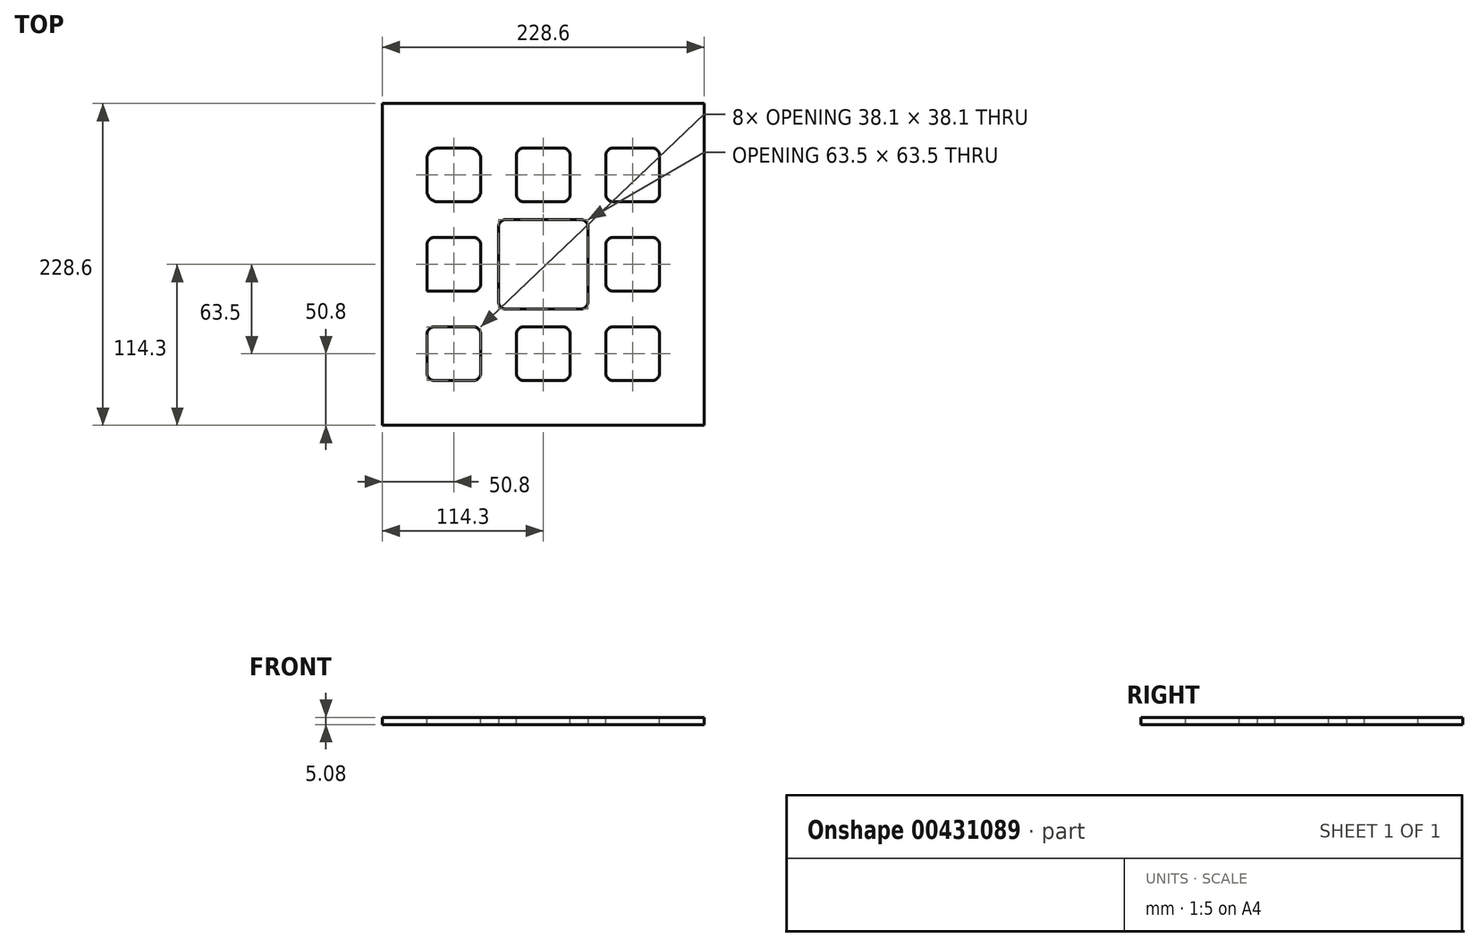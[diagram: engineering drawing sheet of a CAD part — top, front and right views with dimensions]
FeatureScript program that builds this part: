
annotation { "Feature Type Name" : "Feature", "Feature Type Description" : "" }
export const myFeature = defineFeature(function(context is Context, id is Id, definition is map)
    precondition{}
    {
        {
            var Q0;
            Q0=qCreatedBy(makeId("Top.planeOp"),FACE);
            var sketch = newSketch(context, id + "F0", { "sketchPlane" : qUnion([Q0])});
            skLineSegment(sketch, "E0.bottom", {"start": v(114.3, 114.3) * mm, "end": v(-114.3, 114.3) * mm});
            skLineSegment(sketch, "E0.top", {"start": v(114.3, -114.3) * mm, "end": v(-114.3, -114.3) * mm});
            skLineSegment(sketch, "E0.left", {"start": v(114.3, 114.3) * mm, "end": v(114.3, -114.3) * mm});
            skLineSegment(sketch, "E0.right", {"start": v(-114.3, 114.3) * mm, "end": v(-114.3, -114.3) * mm});
            skPoint(sketch, "E0.middle", {"position": v(0, 0) * mm});
            skLineSegment(sketch, "E1.bottom", {"start": v(31.75, 31.75) * mm, "end": v(-31.75, 31.75) * mm});
            skLineSegment(sketch, "E1.top", {"start": v(31.75, -31.75) * mm, "end": v(-31.75, -31.75) * mm});
            skLineSegment(sketch, "E1.left", {"start": v(31.75, 31.75) * mm, "end": v(31.75, -31.75) * mm});
            skLineSegment(sketch, "E1.right", {"start": v(-31.75, 31.75) * mm, "end": v(-31.75, -31.75) * mm});
            skSolve(sketch);
        }
        {
            var Q0;
            Q0 = qSketchRegion(id + "F0", true);
            extrude(context, id + "F1", {"entities" : qUnion([Q0]), "depth" : 5.08 * mm});
        }
        {
            var Q0;
            Q0=makeQuery(id+"F1.opExtrude","CAP_FACE",FACE,{"disambiguationData":[OSD([sQuery(id+"F0.wireOp",EDGE,"E0.bottom"),sQuery(id+"F0.wireOp",EDGE,"E0.top"),sQuery(id+"F0.wireOp",EDGE,"E0.left"),sQuery(id+"F0.wireOp",EDGE,"E0.right"),sQuery(id+"F0.wireOp",EDGE,"E1.bottom"),sQuery(id+"F0.wireOp",EDGE,"E1.top"),sQuery(id+"F0.wireOp",EDGE,"E1.left"),sQuery(id+"F0.wireOp",EDGE,"E1.right")])],"isStart":false});
            var sketch = newSketch(context, id + "F2", { "sketchPlane" : qUnion([Q0])});
            skLineSegment(sketch, "E2.bottom", {"start": v(-44.45, 82.55) * mm, "end": v(-82.55, 82.55) * mm});
            skLineSegment(sketch, "E2.top", {"start": v(-44.45, 44.45) * mm, "end": v(-82.55, 44.45) * mm});
            skLineSegment(sketch, "E2.left", {"start": v(-44.45, 82.55) * mm, "end": v(-44.45, 44.45) * mm});
            skLineSegment(sketch, "E2.right", {"start": v(-82.55, 82.55) * mm, "end": v(-82.55, 44.45) * mm});
            skPoint(sketch, "E2.middle", {"position": v(-63.5, 63.5) * mm});
            skSolve(sketch);
        }
        {
            var Q0;
            Q0 = qSketchRegion(id + "F2", true);
            extrude(context, id + "F3", {"entities" : qUnion([Q0]), "operationType" : NewBodyOperationType.REMOVE, "oppositeDirection" : true, "depth" : 25.4 * mm});
        }
        {
            var Q0;
            Q0=makeQuery(id+"F3.boolean.opBoolean","COPY",EDGE,{"derivedFrom":makeQuery(id+"F3.opExtrude","SWEPT_EDGE",EDGE,{"disambiguationData":[OSD([sQuery(id+"F2.wireOp",EDGE,"E2.bottom"),sQuery(id+"F2.wireOp",EDGE,"E2.right")])]})});
            var Q1;
            Q1=makeQuery(id+"F3.boolean.opBoolean","COPY",EDGE,{"derivedFrom":makeQuery(id+"F3.opExtrude","SWEPT_EDGE",EDGE,{"disambiguationData":[OSD([sQuery(id+"F2.wireOp",EDGE,"E2.bottom"),sQuery(id+"F2.wireOp",EDGE,"E2.left")])]})});
            var Q2;
            Q2=makeQuery(id+"F3.boolean.opBoolean","COPY",EDGE,{"derivedFrom":makeQuery(id+"F3.opExtrude","SWEPT_EDGE",EDGE,{"disambiguationData":[OSD([sQuery(id+"F2.wireOp",EDGE,"E2.top"),sQuery(id+"F2.wireOp",EDGE,"E2.left")])]})});
            var Q3;
            Q3=makeQuery(id+"F3.boolean.opBoolean","COPY",EDGE,{"derivedFrom":makeQuery(id+"F3.opExtrude","SWEPT_EDGE",EDGE,{"disambiguationData":[OSD([sQuery(id+"F2.wireOp",EDGE,"E2.top"),sQuery(id+"F2.wireOp",EDGE,"E2.right")])]})});
            fillet(context, id + "F4", {"entities" : qUnion([Q0, Q1, Q2, Q3]), "radius" : 7.62 * mm, "tangentPropagation" : true, "allowEdgeOverflow" : false});
        }
        {
            var Q0;
            Q0=makeQuery(id+"F1.opExtrude","CAP_FACE",FACE,{"disambiguationData":[OSD([sQuery(id+"F0.wireOp",EDGE,"E0.bottom"),sQuery(id+"F0.wireOp",EDGE,"E0.top"),sQuery(id+"F0.wireOp",EDGE,"E0.left"),sQuery(id+"F0.wireOp",EDGE,"E0.right"),sQuery(id+"F0.wireOp",EDGE,"E1.bottom"),sQuery(id+"F0.wireOp",EDGE,"E1.top"),sQuery(id+"F0.wireOp",EDGE,"E1.left"),sQuery(id+"F0.wireOp",EDGE,"E1.right")])],"isStart":false});
            var sketch = newSketch(context, id + "F5", { "sketchPlane" : qUnion([Q0])});
            skLineSegment(sketch, "E3.bottom", {"start": v(19.05, 82.55) * mm, "end": v(-19.05, 82.55) * mm});
            skLineSegment(sketch, "E3.top", {"start": v(19.05, 44.45) * mm, "end": v(-19.05, 44.45) * mm});
            skLineSegment(sketch, "E3.left", {"start": v(19.05, 82.55) * mm, "end": v(19.05, 44.45) * mm});
            skLineSegment(sketch, "E3.right", {"start": v(-19.05, 82.55) * mm, "end": v(-19.05, 44.45) * mm});
            skPoint(sketch, "E3.middle", {"position": v(0, 63.5) * mm});
            skLineSegment(sketch, "E4.bottom", {"start": v(82.55, 82.55) * mm, "end": v(44.45, 82.55) * mm});
            skLineSegment(sketch, "E4.top", {"start": v(82.55, 44.45) * mm, "end": v(44.45, 44.45) * mm});
            skLineSegment(sketch, "E4.left", {"start": v(82.55, 82.55) * mm, "end": v(82.55, 44.45) * mm});
            skLineSegment(sketch, "E4.right", {"start": v(44.45, 82.55) * mm, "end": v(44.45, 44.45) * mm});
            skPoint(sketch, "E4.middle", {"position": v(63.5, 63.5) * mm});
            skLineSegment(sketch, "E5.bottom", {"start": v(82.55, 19.05) * mm, "end": v(44.45, 19.05) * mm});
            skLineSegment(sketch, "E5.top", {"start": v(82.55, -19.05) * mm, "end": v(44.45, -19.05) * mm});
            skLineSegment(sketch, "E5.left", {"start": v(82.55, 19.05) * mm, "end": v(82.55, -19.05) * mm});
            skLineSegment(sketch, "E5.right", {"start": v(44.45, 19.05) * mm, "end": v(44.45, -19.05) * mm});
            skPoint(sketch, "E5.middle", {"position": v(63.5, 0) * mm});
            skLineSegment(sketch, "E6.bottom", {"start": v(82.55, -44.45) * mm, "end": v(44.45, -44.45) * mm});
            skLineSegment(sketch, "E6.top", {"start": v(82.55, -82.55) * mm, "end": v(44.45, -82.55) * mm});
            skLineSegment(sketch, "E6.left", {"start": v(82.55, -44.45) * mm, "end": v(82.55, -82.55) * mm});
            skLineSegment(sketch, "E6.right", {"start": v(44.45, -44.45) * mm, "end": v(44.45, -82.55) * mm});
            skPoint(sketch, "E6.middle", {"position": v(63.5, -63.5) * mm});
            skLineSegment(sketch, "E7.bottom", {"start": v(19.05, -44.45) * mm, "end": v(-19.05, -44.45) * mm});
            skLineSegment(sketch, "E7.top", {"start": v(19.05, -82.55) * mm, "end": v(-19.05, -82.55) * mm});
            skLineSegment(sketch, "E7.left", {"start": v(19.05, -44.45) * mm, "end": v(19.05, -82.55) * mm});
            skLineSegment(sketch, "E7.right", {"start": v(-19.05, -44.45) * mm, "end": v(-19.05, -82.55) * mm});
            skPoint(sketch, "E7.middle", {"position": v(0, -63.5) * mm});
            skLineSegment(sketch, "E8.bottom", {"start": v(-44.45, -44.45) * mm, "end": v(-82.55, -44.45) * mm});
            skLineSegment(sketch, "E8.top", {"start": v(-44.45, -82.55) * mm, "end": v(-82.55, -82.55) * mm});
            skLineSegment(sketch, "E8.left", {"start": v(-44.45, -44.45) * mm, "end": v(-44.45, -82.55) * mm});
            skLineSegment(sketch, "E8.right", {"start": v(-82.55, -44.45) * mm, "end": v(-82.55, -82.55) * mm});
            skPoint(sketch, "E8.middle", {"position": v(-63.5, -63.5) * mm});
            skLineSegment(sketch, "E9.bottom", {"start": v(-44.45, 19.05) * mm, "end": v(-82.55, 19.05) * mm});
            skLineSegment(sketch, "E9.top", {"start": v(-44.45, -19.05) * mm, "end": v(-82.55, -19.05) * mm});
            skLineSegment(sketch, "E9.left", {"start": v(-44.45, 19.05) * mm, "end": v(-44.45, -19.05) * mm});
            skLineSegment(sketch, "E9.right", {"start": v(-82.55, 19.05) * mm, "end": v(-82.55, -19.05) * mm});
            skPoint(sketch, "E9.middle", {"position": v(-63.5, 0) * mm});
            skSolve(sketch);
        }
        {
            var Q0;
            Q0=makeQuery(id+"F5.imprint","IMPRINT",FACE,{"disambiguationData":[TD([[makeQuery(id+"F5.imprint","IMPRINT",EDGE,{"derivedFrom":sQuery(id+"F5.wireOp",EDGE,"E9.bottom")}),1.0]])]});
            var Q1;
            Q1=makeQuery(id+"F5.imprint","IMPRINT",FACE,{"disambiguationData":[TD([[makeQuery(id+"F5.imprint","IMPRINT",EDGE,{"derivedFrom":sQuery(id+"F5.wireOp",EDGE,"E3.bottom")}),1.0]])]});
            var Q2;
            Q2=makeQuery(id+"F5.imprint","IMPRINT",FACE,{"disambiguationData":[TD([[makeQuery(id+"F5.imprint","IMPRINT",EDGE,{"derivedFrom":sQuery(id+"F5.wireOp",EDGE,"E4.bottom")}),1.0]])]});
            var Q3;
            Q3=makeQuery(id+"F5.imprint","IMPRINT",FACE,{"disambiguationData":[TD([[makeQuery(id+"F5.imprint","IMPRINT",EDGE,{"derivedFrom":sQuery(id+"F5.wireOp",EDGE,"E5.bottom")}),1.0]])]});
            var Q4;
            Q4=makeQuery(id+"F5.imprint","IMPRINT",FACE,{"disambiguationData":[TD([[makeQuery(id+"F5.imprint","IMPRINT",EDGE,{"derivedFrom":sQuery(id+"F5.wireOp",EDGE,"E6.bottom")}),1.0]])]});
            var Q5;
            Q5=makeQuery(id+"F5.imprint","IMPRINT",FACE,{"disambiguationData":[TD([[makeQuery(id+"F5.imprint","IMPRINT",EDGE,{"derivedFrom":sQuery(id+"F5.wireOp",EDGE,"E7.bottom")}),1.0]])]});
            var Q6;
            Q6=makeQuery(id+"F5.imprint","IMPRINT",FACE,{"disambiguationData":[TD([[makeQuery(id+"F5.imprint","IMPRINT",EDGE,{"derivedFrom":sQuery(id+"F5.wireOp",EDGE,"E8.bottom")}),1.0]])]});
            extrude(context, id + "F6", {"entities" : qUnion([Q0, Q1, Q2, Q3, Q4, Q5, Q6]), "operationType" : NewBodyOperationType.REMOVE, "oppositeDirection" : true, "depth" : 25.4 * mm});
        }
        {
            var Q0;
            Q0=makeQuery(id+"F6.boolean.opBoolean","COPY",EDGE,{"derivedFrom":makeQuery(id+"F6.opExtrude","SWEPT_EDGE",EDGE,{"disambiguationData":[OSD([sQuery(id+"F5.wireOp",EDGE,"E9.bottom"),sQuery(id+"F5.wireOp",EDGE,"E9.right")])]})});
            var Q1;
            Q1=makeQuery(id+"F6.boolean.opBoolean","COPY",EDGE,{"derivedFrom":makeQuery(id+"F6.opExtrude","SWEPT_EDGE",EDGE,{"disambiguationData":[OSD([sQuery(id+"F5.wireOp",EDGE,"E8.bottom"),sQuery(id+"F5.wireOp",EDGE,"E8.right")])]})});
            var Q2;
            Q2=makeQuery(id+"F1.opExtrude","SWEPT_EDGE",EDGE,{"disambiguationData":[OSD([sQuery(id+"F0.wireOp",EDGE,"E1.bottom"),sQuery(id+"F0.wireOp",EDGE,"E1.right")])]});
            var Q3;
            Q3=makeQuery(id+"F6.boolean.opBoolean","COPY",EDGE,{"derivedFrom":makeQuery(id+"F6.opExtrude","SWEPT_EDGE",EDGE,{"disambiguationData":[OSD([sQuery(id+"F5.wireOp",EDGE,"E3.bottom"),sQuery(id+"F5.wireOp",EDGE,"E3.right")])]})});
            var Q4;
            Q4=makeQuery(id+"F6.boolean.opBoolean","COPY",EDGE,{"derivedFrom":makeQuery(id+"F6.opExtrude","SWEPT_EDGE",EDGE,{"disambiguationData":[OSD([sQuery(id+"F5.wireOp",EDGE,"E5.bottom"),sQuery(id+"F5.wireOp",EDGE,"E5.right")])]})});
            var Q5;
            Q5=makeQuery(id+"F6.boolean.opBoolean","COPY",EDGE,{"derivedFrom":makeQuery(id+"F6.opExtrude","SWEPT_EDGE",EDGE,{"disambiguationData":[OSD([sQuery(id+"F5.wireOp",EDGE,"E4.bottom"),sQuery(id+"F5.wireOp",EDGE,"E4.right")])]})});
            var Q6;
            Q6=makeQuery(id+"F6.boolean.opBoolean","COPY",EDGE,{"derivedFrom":makeQuery(id+"F6.opExtrude","SWEPT_EDGE",EDGE,{"disambiguationData":[OSD([sQuery(id+"F5.wireOp",EDGE,"E6.bottom"),sQuery(id+"F5.wireOp",EDGE,"E6.right")])]})});
            var Q7;
            Q7=makeQuery(id+"F6.boolean.opBoolean","COPY",EDGE,{"derivedFrom":makeQuery(id+"F6.opExtrude","SWEPT_EDGE",EDGE,{"disambiguationData":[OSD([sQuery(id+"F5.wireOp",EDGE,"E7.bottom"),sQuery(id+"F5.wireOp",EDGE,"E7.right")])]})});
            var Q8;
            Q8=makeQuery(id+"F6.boolean.opBoolean","COPY",EDGE,{"derivedFrom":makeQuery(id+"F6.opExtrude","SWEPT_EDGE",EDGE,{"disambiguationData":[OSD([sQuery(id+"F5.wireOp",EDGE,"E4.bottom"),sQuery(id+"F5.wireOp",EDGE,"E4.left")])]})});
            var Q9;
            Q9=makeQuery(id+"F6.boolean.opBoolean","COPY",EDGE,{"derivedFrom":makeQuery(id+"F6.opExtrude","SWEPT_EDGE",EDGE,{"disambiguationData":[OSD([sQuery(id+"F5.wireOp",EDGE,"E5.bottom"),sQuery(id+"F5.wireOp",EDGE,"E5.left")])]})});
            var Q10;
            Q10=makeQuery(id+"F6.boolean.opBoolean","COPY",EDGE,{"derivedFrom":makeQuery(id+"F6.opExtrude","SWEPT_EDGE",EDGE,{"disambiguationData":[OSD([sQuery(id+"F5.wireOp",EDGE,"E6.bottom"),sQuery(id+"F5.wireOp",EDGE,"E6.left")])]})});
            var Q11;
            Q11=makeQuery(id+"F6.boolean.opBoolean","COPY",EDGE,{"derivedFrom":makeQuery(id+"F6.opExtrude","SWEPT_EDGE",EDGE,{"disambiguationData":[OSD([sQuery(id+"F5.wireOp",EDGE,"E7.bottom"),sQuery(id+"F5.wireOp",EDGE,"E7.left")])]})});
            var Q12;
            Q12=makeQuery(id+"F1.opExtrude","SWEPT_EDGE",EDGE,{"disambiguationData":[OSD([sQuery(id+"F0.wireOp",EDGE,"E1.bottom"),sQuery(id+"F0.wireOp",EDGE,"E1.left")])]});
            var Q13;
            Q13=makeQuery(id+"F6.boolean.opBoolean","COPY",EDGE,{"derivedFrom":makeQuery(id+"F6.opExtrude","SWEPT_EDGE",EDGE,{"disambiguationData":[OSD([sQuery(id+"F5.wireOp",EDGE,"E8.bottom"),sQuery(id+"F5.wireOp",EDGE,"E8.left")])]})});
            var Q14;
            Q14=makeQuery(id+"F6.boolean.opBoolean","COPY",EDGE,{"derivedFrom":makeQuery(id+"F6.opExtrude","SWEPT_EDGE",EDGE,{"disambiguationData":[OSD([sQuery(id+"F5.wireOp",EDGE,"E9.bottom"),sQuery(id+"F5.wireOp",EDGE,"E9.left")])]})});
            var Q15;
            Q15=makeQuery(id+"F6.boolean.opBoolean","COPY",EDGE,{"derivedFrom":makeQuery(id+"F6.opExtrude","SWEPT_EDGE",EDGE,{"disambiguationData":[OSD([sQuery(id+"F5.wireOp",EDGE,"E3.bottom"),sQuery(id+"F5.wireOp",EDGE,"E3.left")])]})});
            var Q16;
            Q16=makeQuery(id+"F6.boolean.opBoolean","COPY",EDGE,{"derivedFrom":makeQuery(id+"F6.opExtrude","SWEPT_EDGE",EDGE,{"disambiguationData":[OSD([sQuery(id+"F5.wireOp",EDGE,"E3.top"),sQuery(id+"F5.wireOp",EDGE,"E3.left")])]})});
            var Q17;
            Q17=makeQuery(id+"F6.boolean.opBoolean","COPY",EDGE,{"derivedFrom":makeQuery(id+"F6.opExtrude","SWEPT_EDGE",EDGE,{"disambiguationData":[OSD([sQuery(id+"F5.wireOp",EDGE,"E5.top"),sQuery(id+"F5.wireOp",EDGE,"E5.left")])]})});
            var Q18;
            Q18=makeQuery(id+"F6.boolean.opBoolean","COPY",EDGE,{"derivedFrom":makeQuery(id+"F6.opExtrude","SWEPT_EDGE",EDGE,{"disambiguationData":[OSD([sQuery(id+"F5.wireOp",EDGE,"E6.top"),sQuery(id+"F5.wireOp",EDGE,"E6.left")])]})});
            var Q19;
            Q19=makeQuery(id+"F6.boolean.opBoolean","COPY",EDGE,{"derivedFrom":makeQuery(id+"F6.opExtrude","SWEPT_EDGE",EDGE,{"disambiguationData":[OSD([sQuery(id+"F5.wireOp",EDGE,"E7.top"),sQuery(id+"F5.wireOp",EDGE,"E7.left")])]})});
            var Q20;
            Q20=makeQuery(id+"F6.boolean.opBoolean","COPY",EDGE,{"derivedFrom":makeQuery(id+"F6.opExtrude","SWEPT_EDGE",EDGE,{"disambiguationData":[OSD([sQuery(id+"F5.wireOp",EDGE,"E8.top"),sQuery(id+"F5.wireOp",EDGE,"E8.left")])]})});
            var Q21;
            Q21=makeQuery(id+"F6.boolean.opBoolean","COPY",EDGE,{"derivedFrom":makeQuery(id+"F6.opExtrude","SWEPT_EDGE",EDGE,{"disambiguationData":[OSD([sQuery(id+"F5.wireOp",EDGE,"E9.top"),sQuery(id+"F5.wireOp",EDGE,"E9.left")])]})});
            var Q22;
            Q22=makeQuery(id+"F1.opExtrude","SWEPT_EDGE",EDGE,{"disambiguationData":[OSD([sQuery(id+"F0.wireOp",EDGE,"E1.top"),sQuery(id+"F0.wireOp",EDGE,"E1.left")])]});
            var Q23;
            Q23=makeQuery(id+"F6.boolean.opBoolean","COPY",EDGE,{"derivedFrom":makeQuery(id+"F6.opExtrude","SWEPT_EDGE",EDGE,{"disambiguationData":[OSD([sQuery(id+"F5.wireOp",EDGE,"E8.top"),sQuery(id+"F5.wireOp",EDGE,"E8.right")])]})});
            var Q24;
            Q24=makeQuery(id+"F6.boolean.opBoolean","COPY",EDGE,{"derivedFrom":makeQuery(id+"F6.opExtrude","SWEPT_EDGE",EDGE,{"disambiguationData":[OSD([sQuery(id+"F5.wireOp",EDGE,"E7.top"),sQuery(id+"F5.wireOp",EDGE,"E7.right")])]})});
            var Q25;
            Q25=makeQuery(id+"F6.boolean.opBoolean","COPY",EDGE,{"derivedFrom":makeQuery(id+"F6.opExtrude","SWEPT_EDGE",EDGE,{"disambiguationData":[OSD([sQuery(id+"F5.wireOp",EDGE,"E6.top"),sQuery(id+"F5.wireOp",EDGE,"E6.right")])]})});
            var Q26;
            Q26=makeQuery(id+"F6.boolean.opBoolean","COPY",EDGE,{"derivedFrom":makeQuery(id+"F6.opExtrude","SWEPT_EDGE",EDGE,{"disambiguationData":[OSD([sQuery(id+"F5.wireOp",EDGE,"E5.top"),sQuery(id+"F5.wireOp",EDGE,"E5.right")])]})});
            var Q27;
            Q27=makeQuery(id+"F6.boolean.opBoolean","COPY",EDGE,{"derivedFrom":makeQuery(id+"F6.opExtrude","SWEPT_EDGE",EDGE,{"disambiguationData":[OSD([sQuery(id+"F5.wireOp",EDGE,"E4.top"),sQuery(id+"F5.wireOp",EDGE,"E4.right")])]})});
            var Q28;
            Q28=makeQuery(id+"F6.boolean.opBoolean","COPY",EDGE,{"derivedFrom":makeQuery(id+"F6.opExtrude","SWEPT_EDGE",EDGE,{"disambiguationData":[OSD([sQuery(id+"F5.wireOp",EDGE,"E3.top"),sQuery(id+"F5.wireOp",EDGE,"E3.right")])]})});
            var Q29;
            Q29=makeQuery(id+"F6.boolean.opBoolean","COPY",EDGE,{"derivedFrom":makeQuery(id+"F6.opExtrude","SWEPT_EDGE",EDGE,{"disambiguationData":[OSD([sQuery(id+"F5.wireOp",EDGE,"E4.top"),sQuery(id+"F5.wireOp",EDGE,"E4.left")])]})});
            fillet(context, id + "F7", {"entities" : qUnion([Q0, Q1, Q2, Q3, Q4, Q5, Q6, Q7, Q8, Q9, Q10, Q11, Q12, Q13, Q14, Q15, Q16, Q17, Q18, Q19, Q20, Q21, Q22, Q23, Q24, Q25, Q26, Q27, Q28, Q29]), "radius" : 5.08 * mm, "tangentPropagation" : true, "allowEdgeOverflow" : false});
        }
        {
            var Q0;
            Q0=makeQuery(id+"F1.opExtrude","SWEPT_EDGE",EDGE,{"disambiguationData":[OSD([sQuery(id+"F0.wireOp",EDGE,"E1.top"),sQuery(id+"F0.wireOp",EDGE,"E1.right")])]});
            fillet(context, id + "F8", {"entities" : qUnion([Q0]), "radius" : 5.08 * mm, "tangentPropagation" : true, "allowEdgeOverflow" : false});
        }
    });
